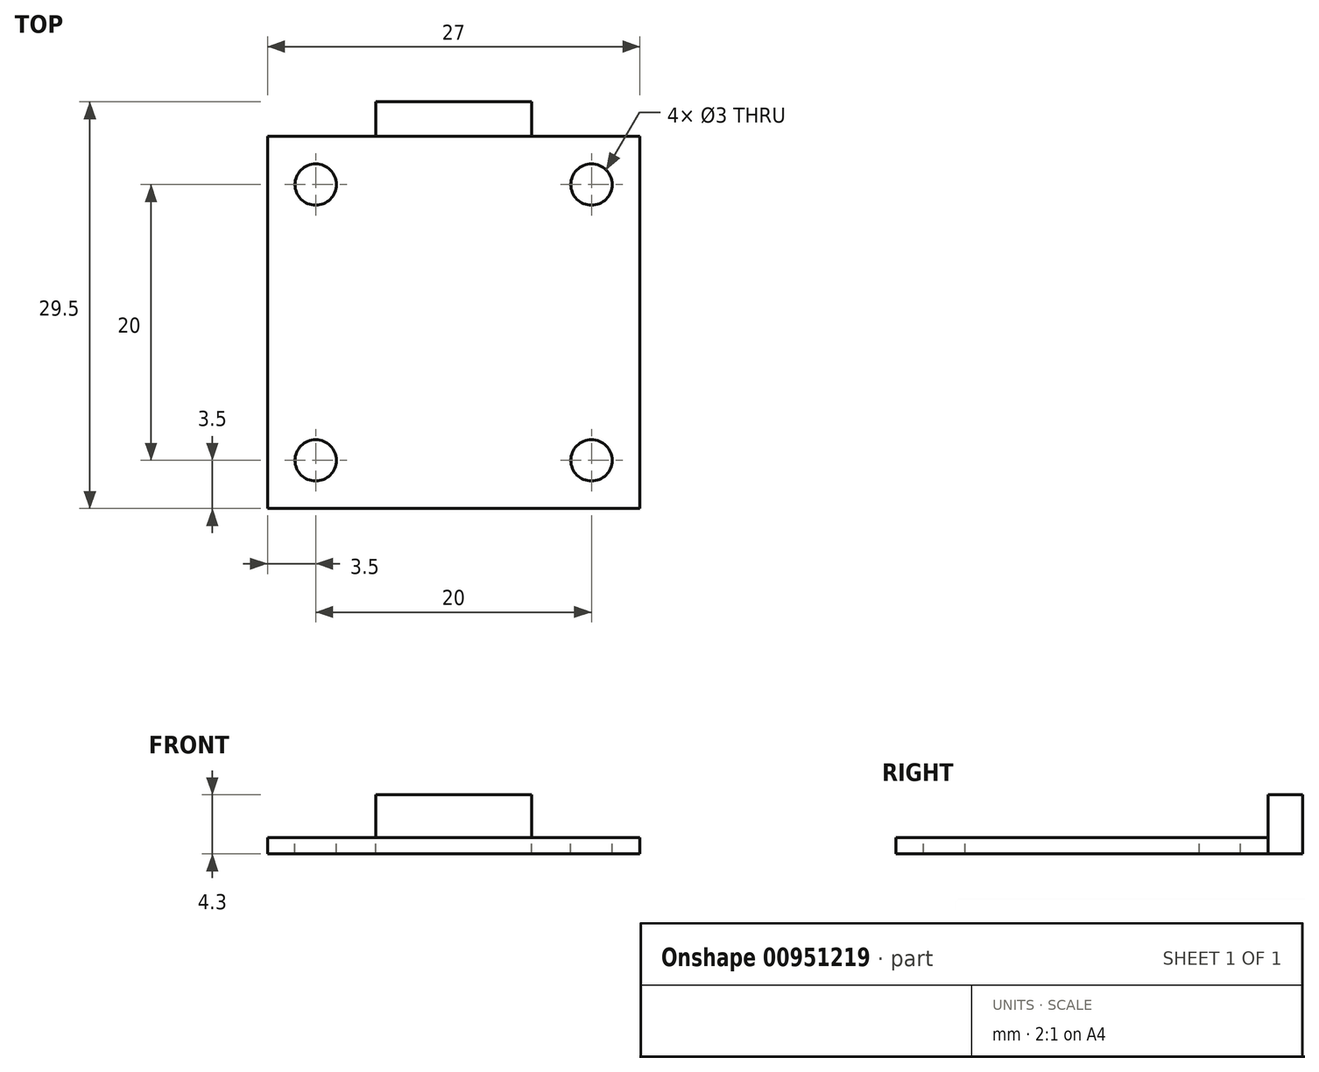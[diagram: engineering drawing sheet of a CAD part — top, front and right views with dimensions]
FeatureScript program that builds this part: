
annotation { "Feature Type Name" : "Feature", "Feature Type Description" : "" }
export const myFeature = defineFeature(function(context is Context, id is Id, definition is map)
    precondition{}
    {
        {
            var Q0;
            Q0=qCreatedBy(makeId("Top.planeOp"),FACE);
            var sketch = newSketch(context, id + "F0", { "sketchPlane" : qUnion([Q0])});
            skLineSegment(sketch, "E0.bottom", {"start": v(-13.5, 13.5) * mm, "end": v(13.5, 13.5) * mm});
            skLineSegment(sketch, "E0.top", {"start": v(-13.5, -13.5) * mm, "end": v(13.5, -13.5) * mm});
            skLineSegment(sketch, "E0.left", {"start": v(-13.5, 13.5) * mm, "end": v(-13.5, -13.5) * mm});
            skLineSegment(sketch, "E0.right", {"start": v(13.5, 13.5) * mm, "end": v(13.5, -13.5) * mm});
            skPoint(sketch, "E0.middle", {"position": v(0, 0) * mm});
            skLineSegment(sketch, "E1", {"start": v(0, 0) * mm, "end": v(0, 13.5) * mm});
            skLineSegment(sketch, "E2", {"start": v(0, 13.5) * mm, "end": v(0, 14.75) * mm});
            skLineSegment(sketch, "E3.bottom", {"start": v(5.65, 13.5) * mm, "end": v(-5.65, 13.5) * mm});
            skLineSegment(sketch, "E3.top", {"start": v(5.65, 16) * mm, "end": v(-5.65, 16) * mm});
            skLineSegment(sketch, "E3.left", {"start": v(5.65, 13.5) * mm, "end": v(5.65, 16) * mm});
            skLineSegment(sketch, "E3.right", {"start": v(-5.65, 13.5) * mm, "end": v(-5.65, 16) * mm});
            skPoint(sketch, "E3.middle", {"position": v(0, 14.75) * mm});
            skCircle(sketch, "E4", {"center": v(-10, 10) * mm, "radius": 1.5 * mm});
            skCircle(sketch, "E5", {"center": v(-10, -10) * mm, "radius": 1.5 * mm});
            skCircle(sketch, "E6", {"center": v(10, -10) * mm, "radius": 1.5 * mm});
            skCircle(sketch, "E7", {"center": v(10, 10) * mm, "radius": 1.5 * mm});
            skSolve(sketch);
        }
        {
            var Q0;
            Q0=makeQuery(id+"F0.imprint","IMPRINT",FACE,{"disambiguationData":[TD([[makeQuery(id+"F0.imprint","IMPRINT",EDGE,{"derivedFrom":sQuery(id+"F0.wireOp",EDGE,"E3.top")}),1.0]])]});
            var Q1;
            Q1=makeQuery(id+"F0.imprint","IMPRINT",FACE,{"disambiguationData":[TD([[makeQuery(id+"F0.imprint","IMPRINT",EDGE,{"derivedFrom":sQuery(id+"F0.wireOp",EDGE,"E0.top")}),1.0]])]});
            extrude(context, id + "F1", {"entities" : qUnion([Q0, Q1]), "oppositeDirection" : true, "depth" : 1.2 * mm, "offsetDistance" : 25 * mm});
        }
        {
            var Q0;
            Q0=makeQuery(id+"F0.imprint","IMPRINT",FACE,{"disambiguationData":[TD([[makeQuery(id+"F0.imprint","IMPRINT",EDGE,{"derivedFrom":sQuery(id+"F0.wireOp",EDGE,"E3.top")}),1.0]])]});
            extrude(context, id + "F2", {"entities" : qUnion([Q0]), "operationType" : NewBodyOperationType.ADD, "depth" : 3.1 * mm, "offsetDistance" : 25 * mm});
        }
    });
